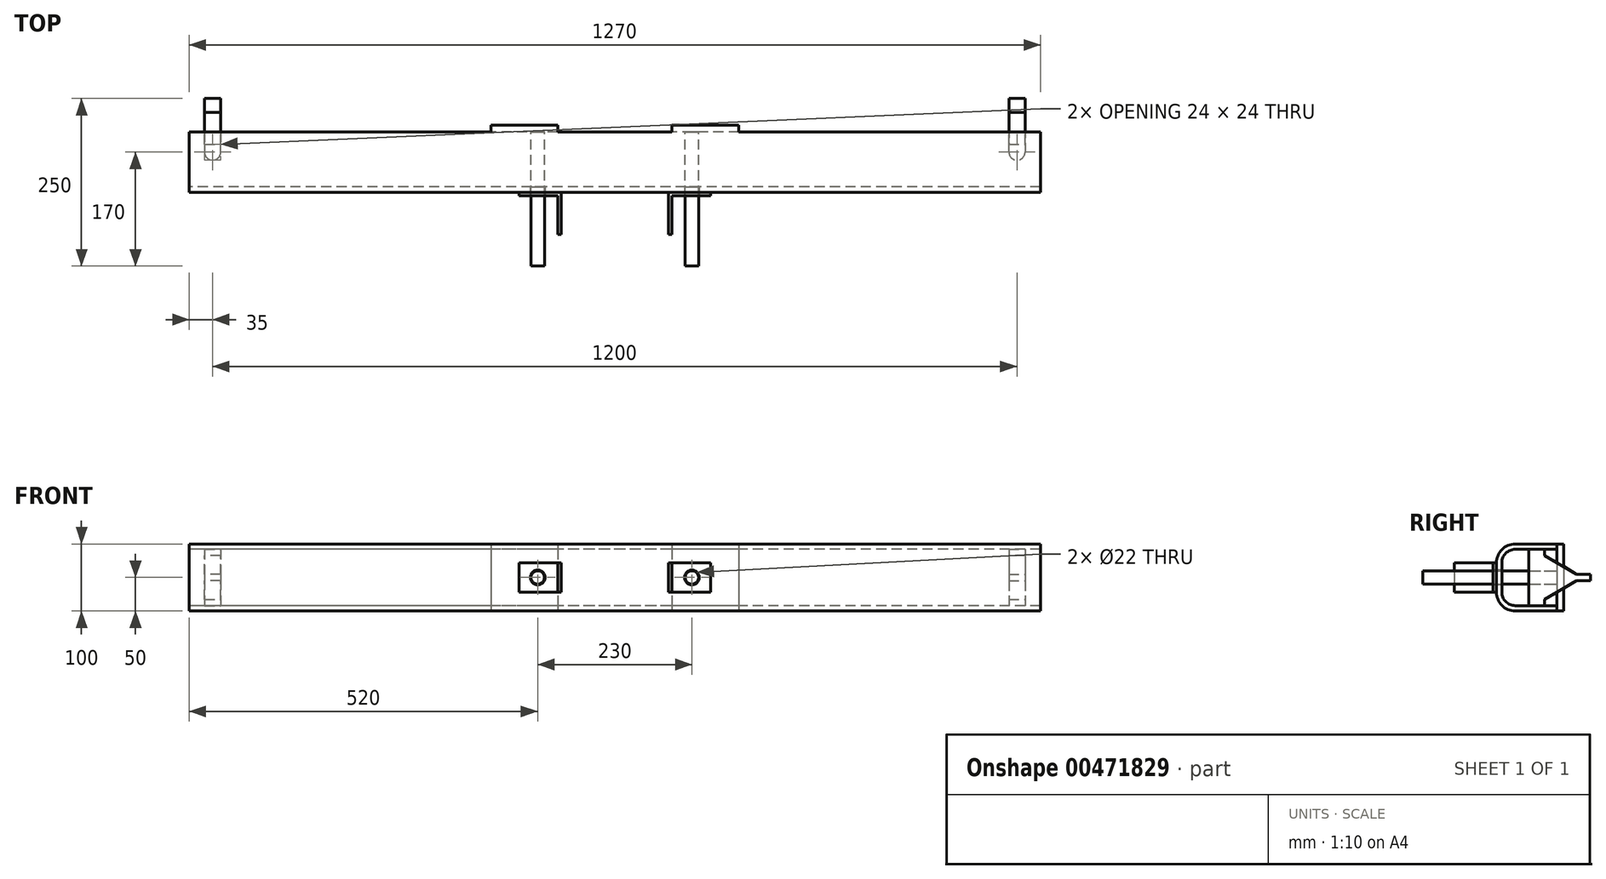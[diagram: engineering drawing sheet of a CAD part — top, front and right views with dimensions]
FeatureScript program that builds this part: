
annotation { "Feature Type Name" : "Feature", "Feature Type Description" : "" }
export const myFeature = defineFeature(function(context is Context, id is Id, definition is map)
    precondition{}
    {
        {
            var Q0;
            Q0=qCreatedBy(makeId("Right.planeOp"),FACE);
            var sketch = newSketch(context, id + "F0", { "sketchPlane" : qUnion([Q0])});
            skLineSegment(sketch, "E0", {"start": v(90, 50) * mm, "end": v(28, 50) * mm});
            skLineSegment(sketch, "E1", {"start": v(0, 22) * mm, "end": v(0, -22) * mm});
            skLineSegment(sketch, "E2", {"start": v(28, -50) * mm, "end": v(90, -50) * mm});
            skLineSegment(sketch, "E3", {"start": v(90, -50) * mm, "end": v(90, -42) * mm});
            skLineSegment(sketch, "E4", {"start": v(90, -42) * mm, "end": v(28, -42) * mm});
            skLineSegment(sketch, "E5", {"start": v(8, -22) * mm, "end": v(8, 22) * mm});
            skLineSegment(sketch, "E6", {"start": v(28, 42) * mm, "end": v(90, 42) * mm});
            skLineSegment(sketch, "E7", {"start": v(90, 42) * mm, "end": v(90, 50) * mm});
            skPoint(sketch, "E8.visualSharp", {"position": v(8, 42) * mm});
            skArc(sketch, "E8.filletArc", {"start": v(28, 42) * mm, "mid": v(13.86, 36.14) * mm, "end": v(8, 22) * mm});
            skPoint(sketch, "E9.visualSharp", {"position": v(8, -42) * mm});
            skArc(sketch, "E9.filletArc", {"start": v(8, -22) * mm, "mid": v(13.86, -36.14) * mm, "end": v(28, -42) * mm});
            skPoint(sketch, "E10.visualSharp", {"position": v(0, 50) * mm});
            skArc(sketch, "E10.filletArc", {"start": v(28, 50) * mm, "mid": v(8.2, 41.8) * mm, "end": v(0, 22) * mm});
            skPoint(sketch, "E11.visualSharp", {"position": v(0, -50) * mm});
            skArc(sketch, "E11.filletArc", {"start": v(0, -22) * mm, "mid": v(8.2, -41.8) * mm, "end": v(28, -50) * mm});
            skSolve(sketch);
        }
        {
            var Q0;
            Q0=qSketchRegion(id+"F0",true);
            extrude(context, id + "F1", {"entities" : qUnion([Q0]), "endBound" : BoundingType.SYMMETRIC, "depth" : 1270 * mm});
        }
        {
            var Q0;
            Q0=qCreatedBy(makeId("Top.planeOp"),FACE);
            var sketch = newSketch(context, id + "F2", { "sketchPlane" : qUnion([Q0])});
            skLineSegment(sketch, "E12", {"start": v(-143, 0) * mm, "end": v(-80, 0) * mm});
            skLineSegment(sketch, "E13", {"start": v(-80, 0) * mm, "end": v(-80, -63) * mm});
            skLineSegment(sketch, "E14.0", {"start": v(-85, -5) * mm, "end": v(-85, -63) * mm});
            skLineSegment(sketch, "E14.1", {"start": v(-143, -5) * mm, "end": v(-85, -5) * mm});
            skLineSegment(sketch, "E15", {"start": v(-143, -5) * mm, "end": v(-143, 0) * mm});
            skLineSegment(sketch, "E16", {"start": v(-85, -63) * mm, "end": v(-80, -63) * mm});
            skLineSegment(sketch, "E17.MirrorCS", {"start": v(85, -63) * mm, "end": v(80, -63) * mm});
            skLineSegment(sketch, "E18.MirrorCS", {"start": v(143, -5) * mm, "end": v(143, 0) * mm});
            skLineSegment(sketch, "E19.MirrorCS", {"start": v(143, 0) * mm, "end": v(80, 0) * mm});
            skLineSegment(sketch, "E20.MirrorCS", {"start": v(80, 0) * mm, "end": v(80, -63) * mm});
            skLineSegment(sketch, "E21.MirrorCS", {"start": v(143, -5) * mm, "end": v(85, -5) * mm});
            skLineSegment(sketch, "E22.MirrorCS", {"start": v(85, -5) * mm, "end": v(85, -63) * mm});
            skSolve(sketch);
        }
        {
            var Q0;
            Q0=qSketchRegion(id+"F2",true);
            extrude(context, id + "F3", {"entities" : qUnion([Q0]), "operationType" : NewBodyOperationType.ADD, "endBound" : BoundingType.SYMMETRIC, "depth" : 44 * mm});
        }
        {
            var Q0;
            Q0=makeQuery(id+"F1.opExtrude","SWEPT_FACE",FACE,{"disambiguationData":[OSD([sQuery(id+"F0.wireOp",EDGE,"E7")])]});
            var sketch = newSketch(context, id + "F4", { "sketchPlane" : qUnion([Q0])});
            skLineSegment(sketch, "E23.bottom", {"start": v(-185, 50) * mm, "end": v(-85, 50) * mm});
            skLineSegment(sketch, "E23.top", {"start": v(-185, -50) * mm, "end": v(-85, -50) * mm});
            skLineSegment(sketch, "E23.left", {"start": v(-185, 50) * mm, "end": v(-185, -50) * mm});
            skLineSegment(sketch, "E23.right", {"start": v(-85, 50) * mm, "end": v(-85, -50) * mm});
            skLineSegment(sketch, "E24.MirrorCS", {"start": v(85, 50) * mm, "end": v(85, -50) * mm});
            skLineSegment(sketch, "E25.MirrorCS", {"start": v(185, 50) * mm, "end": v(185, -50) * mm});
            skLineSegment(sketch, "E26.MirrorCS", {"start": v(185, 50) * mm, "end": v(85, 50) * mm});
            skLineSegment(sketch, "E27.MirrorCS", {"start": v(185, -50) * mm, "end": v(85, -50) * mm});
            skSolve(sketch);
        }
        {
            var Q0;
            Q0=qSketchRegion(id+"F4",true);
            extrude(context, id + "F5", {"entities" : qUnion([Q0]), "operationType" : NewBodyOperationType.ADD, "depth" : 10 * mm});
        }
        {
            var Q0;
            Q0=qCreatedBy(makeId("Front.planeOp"),FACE);
            var sketch = newSketch(context, id + "F6", { "sketchPlane" : qUnion([Q0])});
            skCircle(sketch, "E28", {"center": v(-115, 0) * mm, "radius": 11 * mm});
            skCircle(sketch, "E29.MirrorC", {"center": v(115, 0) * mm, "radius": 11 * mm});
            skSolve(sketch);
        }
        {
            var Q0;
            Q0=qSketchRegion(id+"F6",true);
            extrude(context, id + "F7", {"entities" : qUnion([Q0]), "operationType" : NewBodyOperationType.REMOVE, "endBound" : BoundingType.UP_TO_NEXT, "oppositeDirection" : true, "depth" : 25 * mm, "hasSecondDirection" : true, "secondDirectionBound" : SecondDirectionBoundingType.THROUGH_ALL, "secondDirectionOppositeDirection" : false, "secondDirectionDepth" : 25 * mm});
        }
        {
            var Q0;
            Q0=qCreatedBy(makeId("Top.planeOp"),FACE);
            var sketch = newSketch(context, id + "F8", { "sketchPlane" : qUnion([Q0])});
            skArc(sketch, "E30", {"start": v(-612, 60) * mm, "mid": v(-600, 48) * mm, "end": v(-588, 60) * mm});
            skArc(sketch, "E31.MirrorC", {"start": v(612, 60) * mm, "mid": v(600, 48) * mm, "end": v(588, 60) * mm});
            skLineSegment(sketch, "E32", {"start": v(-612, 60) * mm, "end": v(-612, 72) * mm});
            skLineSegment(sketch, "E33", {"start": v(-612, 72) * mm, "end": v(-588, 72) * mm});
            skLineSegment(sketch, "E34", {"start": v(-588, 72) * mm, "end": v(-588, 60) * mm});
            skLineSegment(sketch, "E35.MirrorCS", {"start": v(588, 72) * mm, "end": v(588, 60) * mm});
            skLineSegment(sketch, "E36.MirrorCS", {"start": v(612, 60) * mm, "end": v(612, 72) * mm});
            skLineSegment(sketch, "E37.MirrorCS", {"start": v(612, 72) * mm, "end": v(588, 72) * mm});
            skSolve(sketch);
        }
        {
            var Q0;
            Q0=qSketchRegion(id+"F8",true);
            var Q1;
            Q1=makeQuery(id+"F5.boolean.opBoolean","MERGE",FACE,{"derivedFrom":[makeQuery(id+"F1.opExtrude","SWEPT_FACE",FACE,{"disambiguationData":[OSD([sQuery(id+"F0.wireOp",EDGE,"E2")])]}),makeQuery(id+"F5.opExtrude","SWEPT_FACE",FACE,{"disambiguationData":[OSD([sQuery(id+"F4.wireOp",EDGE,"E23.top")])]}),makeQuery(id+"F5.opExtrude","SWEPT_FACE",FACE,{"disambiguationData":[OSD([sQuery(id+"F4.wireOp",EDGE,"E27.MirrorCS")])]})]});
            extrude(context, id + "F9", {"entities" : qUnion([Q0]), "operationType" : NewBodyOperationType.ADD, "endBoundEntityFace" : qUnion([Q1]), "depth" : 50 * mm, "hasSecondDirection" : true, "secondDirectionOppositeDirection" : true, "secondDirectionDepth" : 50 * mm});
        }
        {
            var Q0;
            Q0=makeQuery(id+"F5.opExtrude","CAP_FACE",FACE,{"disambiguationData":[OSD([sQuery(id+"F4.wireOp",EDGE,"E24.MirrorCS"),sQuery(id+"F4.wireOp",EDGE,"E25.MirrorCS"),sQuery(id+"F4.wireOp",EDGE,"E26.MirrorCS"),sQuery(id+"F4.wireOp",EDGE,"E27.MirrorCS")])],"isStart":true});
            var sketch = newSketch(context, id + "F10", { "sketchPlane" : qUnion([Q0])});
            skCircle(sketch, "E38", {"center": v(-115, 0) * mm, "radius": 10 * mm});
            skCircle(sketch, "E39.MirrorC", {"center": v(115, 0) * mm, "radius": 10 * mm});
            skSolve(sketch);
        }
        {
            var Q0;
            Q0=qSketchRegion(id+"F10",true);
            extrude(context, id + "F11", {"entities" : qUnion([Q0]), "operationType" : NewBodyOperationType.ADD, "depth" : 200 * mm});
        }
        {
            var Q0;
            Q0=qCreatedBy(makeId("Right.planeOp"),FACE);
            cPlane(context, id + "F12", {"entities" : qUnion([Q0]), "cplaneType" : CPlaneType.OFFSET, "offset" : 600 * mm, "width" : 150 * mm, "height" : 150 * mm});
        }
        {
            var Q0;
            Q0=qCreatedBy(id+"F12.planeOp",FACE);
            var sketch = newSketch(context, id + "F13", { "sketchPlane" : qUnion([Q0])});
            skLineSegment(sketch, "E40", {"start": v(60, -40) * mm, "end": v(60, 40) * mm});
            skLineSegment(sketch, "E41", {"start": v(60, 40) * mm, "end": v(128, 0) * mm});
            skLineSegment(sketch, "E42", {"start": v(128, 0) * mm, "end": v(60, -40) * mm});
            skLineSegment(sketch, "E43", {"start": v(0, 0) * mm, "end": v(156.79, 0) * mm, "construction": true});
            skSolve(sketch);
        }
        {
            var Q0;
            Q0=qSketchRegion(id+"F13",true);
            extrude(context, id + "F14", {"entities" : qUnion([Q0]), "operationType" : NewBodyOperationType.ADD, "depth" : 12 * mm, "hasSecondDirection" : true, "secondDirectionOppositeDirection" : true, "secondDirectionDepth" : 12 * mm});
        }
        {
            var Q0;
            Q0=qCreatedBy(makeId("Right.planeOp"),FACE);
            cPlane(context, id + "F15", {"entities" : qUnion([Q0]), "cplaneType" : CPlaneType.OFFSET, "offset" : 600 * mm, "oppositeDirection" : true, "width" : 150 * mm, "height" : 150 * mm});
        }
        {
            var Q0;
            Q0=qCreatedBy(id+"F15.planeOp",FACE);
            var sketch = newSketch(context, id + "F16", { "sketchPlane" : qUnion([Q0])});
            skLineSegment(sketch, "E44", {"start": v(128, 0) * mm, "end": v(60, 40) * mm});
            skLineSegment(sketch, "E45", {"start": v(60, 40) * mm, "end": v(60, -40) * mm});
            skLineSegment(sketch, "E46", {"start": v(60, -40) * mm, "end": v(128, 0) * mm});
            skSolve(sketch);
        }
        {
            var Q0;
            Q0=qSketchRegion(id+"F16",true);
            extrude(context, id + "F17", {"entities" : qUnion([Q0]), "operationType" : NewBodyOperationType.ADD, "depth" : 12 * mm, "hasSecondDirection" : true, "secondDirectionOppositeDirection" : true, "secondDirectionDepth" : 12 * mm});
        }
        {
            var Q0;
            Q0=qCreatedBy(makeId("Top.planeOp"),FACE);
            var sketch = newSketch(context, id + "F18", { "sketchPlane" : qUnion([Q0])});
            skLineSegment(sketch, "E47.bottom", {"start": v(-612, 110) * mm, "end": v(-588, 110) * mm});
            skLineSegment(sketch, "E47.top", {"start": v(-612, 140) * mm, "end": v(-588, 140) * mm});
            skLineSegment(sketch, "E47.left", {"start": v(-612, 110) * mm, "end": v(-612, 140) * mm});
            skLineSegment(sketch, "E47.right", {"start": v(-588, 110) * mm, "end": v(-588, 140) * mm});
            skLineSegment(sketch, "E48.MirrorCS", {"start": v(588, 110) * mm, "end": v(588, 140) * mm});
            skLineSegment(sketch, "E49.MirrorCS", {"start": v(612, 110) * mm, "end": v(612, 140) * mm});
            skLineSegment(sketch, "E50.MirrorCS", {"start": v(612, 110) * mm, "end": v(588, 110) * mm});
            skLineSegment(sketch, "E51.MirrorCS", {"start": v(612, 140) * mm, "end": v(588, 140) * mm});
            skSolve(sketch);
        }
        {
            var Q0;
            Q0=qSketchRegion(id+"F18",true);
            extrude(context, id + "F19", {"entities" : qUnion([Q0]), "operationType" : NewBodyOperationType.ADD, "endBound" : BoundingType.SYMMETRIC, "depth" : 10 * mm});
        }
    });
